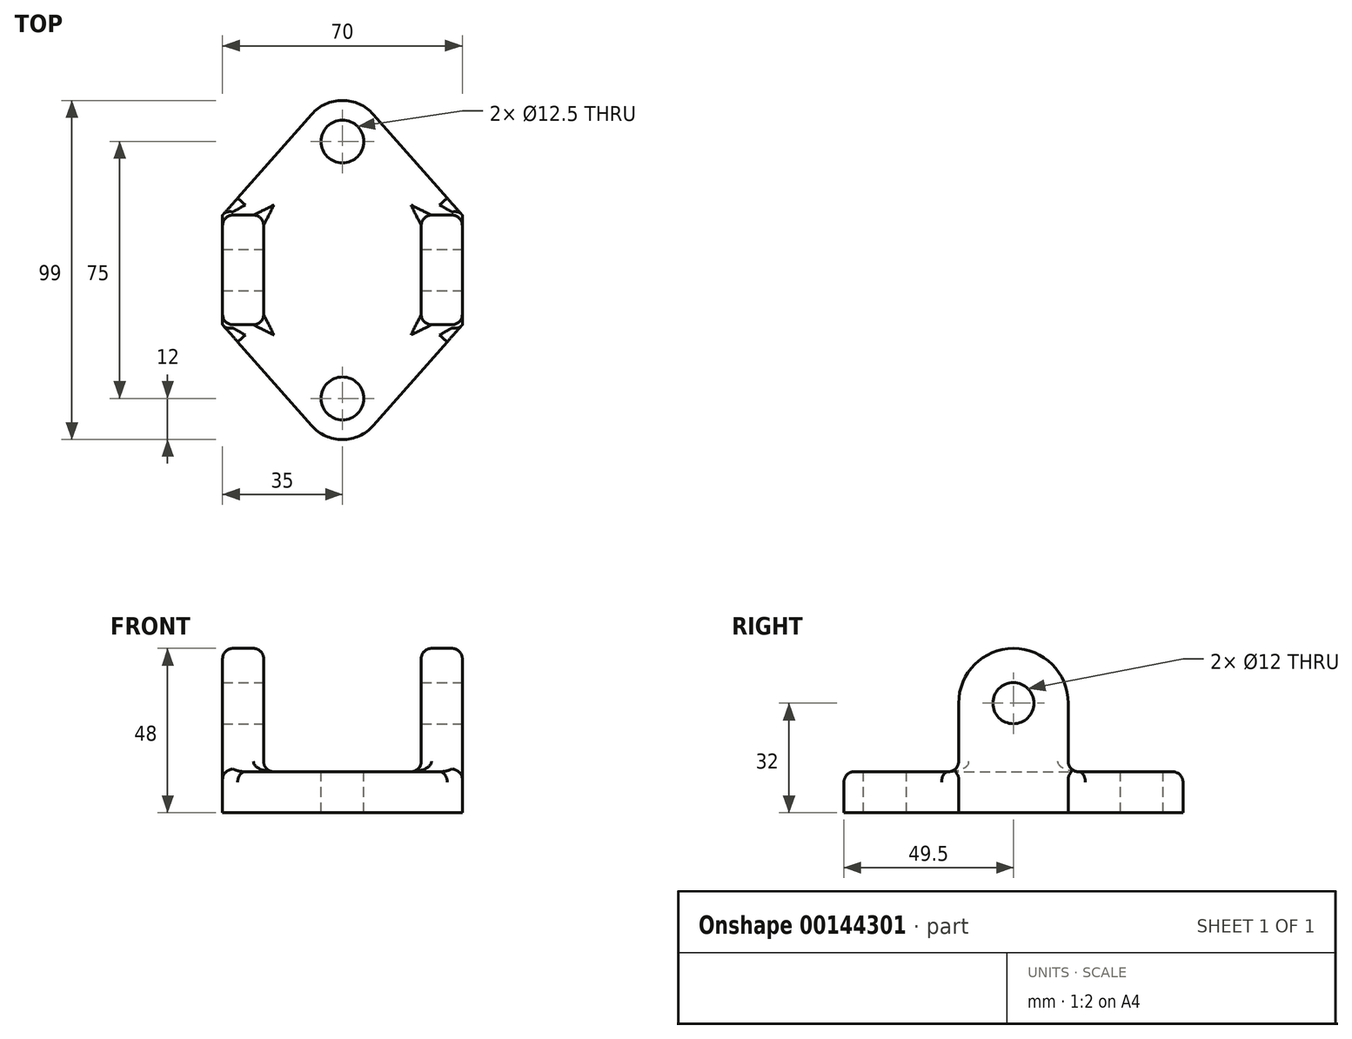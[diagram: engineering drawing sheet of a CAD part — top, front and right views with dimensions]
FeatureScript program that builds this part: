
annotation { "Feature Type Name" : "Feature", "Feature Type Description" : "" }
export const myFeature = defineFeature(function(context is Context, id is Id, definition is map)
    precondition{}
    {
        {
            var Q0;
            Q0=qCreatedBy(makeId("Right.planeOp"),FACE);
            var sketch = newSketch(context, id + "F0", { "sketchPlane" : qUnion([Q0])});
            skLineSegment(sketch, "E0.bottom", {"start": v(-16, 0) * mm, "end": v(16, 0) * mm});
            skLineSegment(sketch, "E0.left", {"start": v(-16, 0) * mm, "end": v(-16, 32) * mm});
            skLineSegment(sketch, "E0.right", {"start": v(16, 0) * mm, "end": v(16, 32) * mm});
            skArc(sketch, "E1", {"start": v(16, 32) * mm, "mid": v(0, 48) * mm, "end": v(-16, 32) * mm});
            skCircle(sketch, "E2", {"center": v(0, 32) * mm, "radius": 6 * mm});
            skSolve(sketch);
        }
        {
            var Q0;
            Q0 = qSketchRegion(id + "F0", true);
            extrude(context, id + "F1", {"entities" : qUnion([Q0]), "oppositeDirection" : true, "depth" : 12 * mm});
        }
        {
            var Q0;
            Q0=qCreatedBy(makeId("Top.planeOp"),FACE);
            var sketch = newSketch(context, id + "F2", { "sketchPlane" : qUnion([Q0])});
            skLineSegment(sketch, "E3", {"start": v(-12, 16) * mm, "end": v(14, 45.44) * mm});
            skLineSegment(sketch, "E4", {"start": v(-12, -16) * mm, "end": v(14, -45.44) * mm});
            skLineSegment(sketch, "E5", {"start": v(32, -45.44) * mm, "end": v(58, -16) * mm});
            skLineSegment(sketch, "E6", {"start": v(58, -16) * mm, "end": v(58, 16) * mm});
            skLineSegment(sketch, "E7", {"start": v(58, 16) * mm, "end": v(32, 45.44) * mm});
            skArc(sketch, "E8", {"start": v(32, 45.44) * mm, "mid": v(23, 49.5) * mm, "end": v(14, 45.44) * mm});
            skArc(sketch, "E9", {"start": v(14, -45.44) * mm, "mid": v(23, -49.5) * mm, "end": v(32, -45.44) * mm});
            skLineSegment(sketch, "E10", {"start": v(23, 37.5) * mm, "end": v(23, -37.5) * mm, "construction": true});
            skLineSegment(sketch, "E11", {"start": v(-12, 0) * mm, "end": v(58, 0) * mm, "construction": true});
            skLineSegment(sketch, "E12", {"start": v(-12, 16) * mm, "end": v(58, 16) * mm, "construction": true});
            skLineSegment(sketch, "E13", {"start": v(58, -16) * mm, "end": v(-12, -16) * mm, "construction": true});
            skLineSegment(sketch, "E14", {"start": v(-12, 16) * mm, "end": v(-12, -16) * mm});
            skSolve(sketch);
        }
        {
            var Q0;
            Q0 = qSketchRegion(id + "F2", true);
            extrude(context, id + "F3", {"entities" : qUnion([Q0]), "operationType" : NewBodyOperationType.ADD, "depth" : 12 * mm});
        }
        {
            var Q0;
            Q0=makeQuery(id+"F3.opExtrude","SWEPT_FACE",FACE,{"disambiguationData":[OSD([sQuery(id+"F2.wireOp",EDGE,"E6")])]});
            var sketch = newSketch(context, id + "F4", { "sketchPlane" : qUnion([Q0])});
            skCircle(sketch, "E15.0", {"center": v(0, 32) * mm, "radius": 6 * mm});
            skArc(sketch, "E16.0", {"start": v(16, 32) * mm, "mid": v(0, 48) * mm, "end": v(-16, 32) * mm});
            skLineSegment(sketch, "E17.0", {"start": v(-16, 12) * mm, "end": v(-16, 32) * mm});
            skLineSegment(sketch, "E18.0", {"start": v(-16, 0) * mm, "end": v(16, 0) * mm});
            skLineSegment(sketch, "E19.0", {"start": v(16, 12) * mm, "end": v(16, 32) * mm});
            skLineSegment(sketch, "E20.0", {"start": v(-16, 0) * mm, "end": v(-16, 12) * mm});
            skLineSegment(sketch, "E21.0", {"start": v(16, 0) * mm, "end": v(16, 12) * mm});
            skSolve(sketch);
        }
        {
            var Q0;
            Q0 = qSketchRegion(id + "F4", true);
            extrude(context, id + "F5", {"entities" : qUnion([Q0]), "operationType" : NewBodyOperationType.ADD, "oppositeDirection" : true, "depth" : 12 * mm});
        }
        {
            var Q0;
            Q0=makeQuery(id+"F3.opExtrude","CAP_FACE",FACE,{"disambiguationData":[OSD([sQuery(id+"F2.wireOp",EDGE,"E3"),sQuery(id+"F2.wireOp",EDGE,"E4"),sQuery(id+"F2.wireOp",EDGE,"E5"),sQuery(id+"F2.wireOp",EDGE,"E6"),sQuery(id+"F2.wireOp",EDGE,"E7"),sQuery(id+"F2.wireOp",EDGE,"E8"),sQuery(id+"F2.wireOp",EDGE,"E9"),sQuery(id+"F2.wireOp",EDGE,"E14")])],"isStart":false});
            var sketch = newSketch(context, id + "F6", { "sketchPlane" : qUnion([Q0])});
            skCircle(sketch, "E22", {"center": v(23, 37.5) * mm, "radius": 6.25 * mm});
            skCircle(sketch, "E23", {"center": v(23, -37.5) * mm, "radius": 6.25 * mm});
            skSolve(sketch);
        }
        {
            var Q0;
            Q0 = qSketchRegion(id + "F6", true);
            extrude(context, id + "F7", {"entities" : qUnion([Q0]), "operationType" : NewBodyOperationType.REMOVE, "oppositeDirection" : true, "depth" : 12 * mm});
        }
        {
            var Q0;
            Q0=makeQuery(id+"F3.boolean.opBoolean","INTERSECT",EDGE,{"derivedFrom":[makeQuery(id+"F1.opExtrude","SWEPT_FACE",FACE,{"disambiguationData":[OSD([sQuery(id+"F0.wireOp",EDGE,"E0.left")])]}),makeQuery(id+"F3.opExtrude","CAP_FACE",FACE,{"disambiguationData":[OSD([sQuery(id+"F2.wireOp",EDGE,"E3"),sQuery(id+"F2.wireOp",EDGE,"E4"),sQuery(id+"F2.wireOp",EDGE,"E5"),sQuery(id+"F2.wireOp",EDGE,"E6"),sQuery(id+"F2.wireOp",EDGE,"E7"),sQuery(id+"F2.wireOp",EDGE,"E8"),sQuery(id+"F2.wireOp",EDGE,"E9"),sQuery(id+"F2.wireOp",EDGE,"E14")])],"isStart":false})]});
            var Q1;
            Q1=makeQuery(id+"F5.boolean.opBoolean","INTERSECT",EDGE,{"derivedFrom":[makeQuery(id+"F3.opExtrude","CAP_FACE",FACE,{"disambiguationData":[OSD([sQuery(id+"F2.wireOp",EDGE,"E3"),sQuery(id+"F2.wireOp",EDGE,"E4"),sQuery(id+"F2.wireOp",EDGE,"E5"),sQuery(id+"F2.wireOp",EDGE,"E6"),sQuery(id+"F2.wireOp",EDGE,"E7"),sQuery(id+"F2.wireOp",EDGE,"E8"),sQuery(id+"F2.wireOp",EDGE,"E9"),sQuery(id+"F2.wireOp",EDGE,"E14")])],"isStart":false}),makeQuery(id+"F5.opExtrude","SWEPT_FACE",FACE,{"disambiguationData":[OSD([sQuery(id+"F4.wireOp",EDGE,"E17.0"),sQuery(id+"F4.wireOp",EDGE,"E20.0")])]})]});
            var Q2;
            Q2=makeQuery(id+"F5.boolean.opBoolean","INTERSECT",EDGE,{"derivedFrom":[makeQuery(id+"F3.opExtrude","CAP_FACE",FACE,{"disambiguationData":[OSD([sQuery(id+"F2.wireOp",EDGE,"E3"),sQuery(id+"F2.wireOp",EDGE,"E4"),sQuery(id+"F2.wireOp",EDGE,"E5"),sQuery(id+"F2.wireOp",EDGE,"E6"),sQuery(id+"F2.wireOp",EDGE,"E7"),sQuery(id+"F2.wireOp",EDGE,"E8"),sQuery(id+"F2.wireOp",EDGE,"E9"),sQuery(id+"F2.wireOp",EDGE,"E14")])],"isStart":false}),makeQuery(id+"F5.opExtrude","CAP_FACE",FACE,{"disambiguationData":[OSD([sQuery(id+"F4.wireOp",EDGE,"E15.0"),sQuery(id+"F4.wireOp",EDGE,"E16.0"),sQuery(id+"F4.wireOp",EDGE,"E17.0"),sQuery(id+"F4.wireOp",EDGE,"E18.0"),sQuery(id+"F4.wireOp",EDGE,"E19.0"),sQuery(id+"F4.wireOp",EDGE,"E20.0"),sQuery(id+"F4.wireOp",EDGE,"E21.0")])],"isStart":false})]});
            var Q3;
            Q3=makeQuery(id+"F3.boolean.opBoolean","INTERSECT",EDGE,{"derivedFrom":[makeQuery(id+"F1.opExtrude","CAP_FACE",FACE,{"disambiguationData":[OSD([sQuery(id+"F0.wireOp",EDGE,"E0.bottom"),sQuery(id+"F0.wireOp",EDGE,"E0.left"),sQuery(id+"F0.wireOp",EDGE,"E0.right"),sQuery(id+"F0.wireOp",EDGE,"E1"),sQuery(id+"F0.wireOp",EDGE,"E2")])],"isStart":true}),makeQuery(id+"F3.opExtrude","CAP_FACE",FACE,{"disambiguationData":[OSD([sQuery(id+"F2.wireOp",EDGE,"E3"),sQuery(id+"F2.wireOp",EDGE,"E4"),sQuery(id+"F2.wireOp",EDGE,"E5"),sQuery(id+"F2.wireOp",EDGE,"E6"),sQuery(id+"F2.wireOp",EDGE,"E7"),sQuery(id+"F2.wireOp",EDGE,"E8"),sQuery(id+"F2.wireOp",EDGE,"E9"),sQuery(id+"F2.wireOp",EDGE,"E14")])],"isStart":false})]});
            var Q4;
            Q4=makeQuery(id+"F3.boolean.opBoolean","INTERSECT",EDGE,{"derivedFrom":[makeQuery(id+"F1.opExtrude","SWEPT_FACE",FACE,{"disambiguationData":[OSD([sQuery(id+"F0.wireOp",EDGE,"E0.right")])]}),makeQuery(id+"F3.opExtrude","CAP_FACE",FACE,{"disambiguationData":[OSD([sQuery(id+"F2.wireOp",EDGE,"E3"),sQuery(id+"F2.wireOp",EDGE,"E4"),sQuery(id+"F2.wireOp",EDGE,"E5"),sQuery(id+"F2.wireOp",EDGE,"E6"),sQuery(id+"F2.wireOp",EDGE,"E7"),sQuery(id+"F2.wireOp",EDGE,"E8"),sQuery(id+"F2.wireOp",EDGE,"E9"),sQuery(id+"F2.wireOp",EDGE,"E14")])],"isStart":false})]});
            var Q5;
            Q5=makeQuery(id+"F5.boolean.opBoolean","INTERSECT",EDGE,{"derivedFrom":[makeQuery(id+"F3.opExtrude","CAP_FACE",FACE,{"disambiguationData":[OSD([sQuery(id+"F2.wireOp",EDGE,"E3"),sQuery(id+"F2.wireOp",EDGE,"E4"),sQuery(id+"F2.wireOp",EDGE,"E5"),sQuery(id+"F2.wireOp",EDGE,"E6"),sQuery(id+"F2.wireOp",EDGE,"E7"),sQuery(id+"F2.wireOp",EDGE,"E8"),sQuery(id+"F2.wireOp",EDGE,"E9"),sQuery(id+"F2.wireOp",EDGE,"E14")])],"isStart":false}),makeQuery(id+"F5.opExtrude","SWEPT_FACE",FACE,{"disambiguationData":[OSD([sQuery(id+"F4.wireOp",EDGE,"E19.0"),sQuery(id+"F4.wireOp",EDGE,"E21.0")])]})]});
            fillet(context, id + "F8", {"entities" : qUnion([Q0, Q1, Q2, Q3, Q4, Q5]), "radius" : 3 * mm, "tangentPropagation" : true, "allowEdgeOverflow" : false});
        }
        {
            var Q0;
            Q0=makeQuery(id+"F1.opExtrude","CAP_EDGE",EDGE,{"disambiguationData":[OSD([sQuery(id+"F0.wireOp",EDGE,"E1")])],"isStart":true});
            var Q1;
            Q1=makeQuery(id+"F5.opExtrude","CAP_EDGE",EDGE,{"disambiguationData":[OSD([sQuery(id+"F4.wireOp",EDGE,"E16.0")])],"isStart":false});
            var Q2;
            Q2=makeQuery(id+"F3.opExtrude","CAP_EDGE",EDGE,{"disambiguationData":[OSD([sQuery(id+"F2.wireOp",EDGE,"E3")])],"isStart":false});
            var Q3;
            Q3=makeQuery(id+"F3.opExtrude","CAP_EDGE",EDGE,{"disambiguationData":[OSD([sQuery(id+"F2.wireOp",EDGE,"E4")])],"isStart":false});
            fillet(context, id + "F9", {"entities" : qUnion([Q0, Q1, Q2, Q3]), "radius" : 3 * mm, "tangentPropagation" : true, "allowEdgeOverflow" : false});
        }
    });
